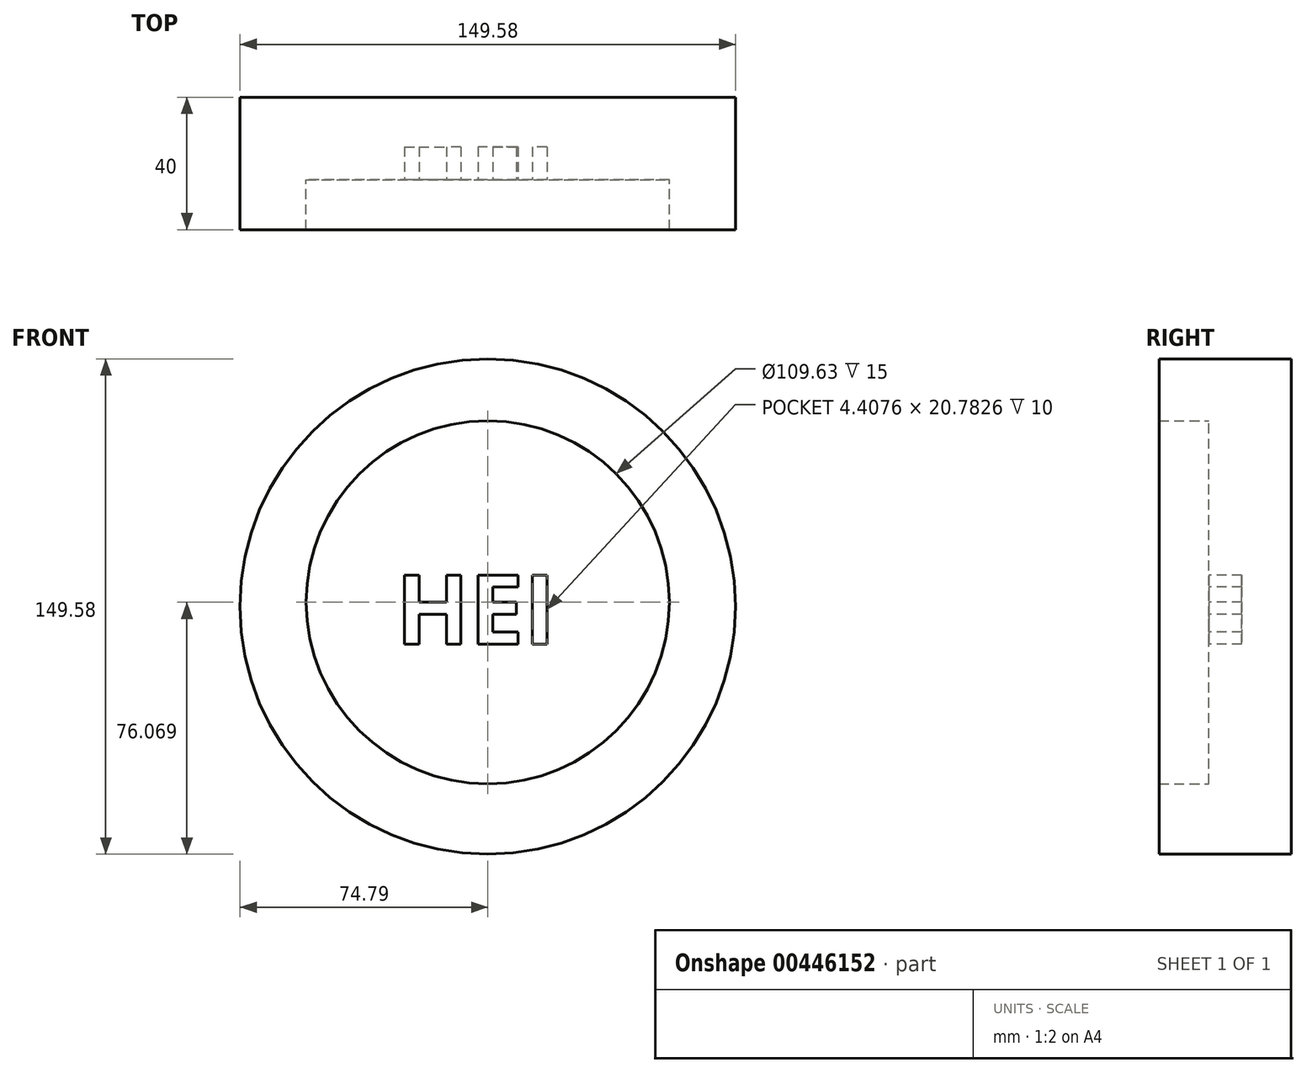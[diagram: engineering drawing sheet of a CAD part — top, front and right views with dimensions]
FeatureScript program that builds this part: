
annotation { "Feature Type Name" : "Feature", "Feature Type Description" : "" }
export const myFeature = defineFeature(function(context is Context, id is Id, definition is map)
    precondition{}
    {
        {
            var Q0;
            Q0=qCreatedBy(makeId("Front.planeOp"),FACE);
            var sketch = newSketch(context, id + "F0", { "sketchPlane" : qUnion([Q0])});
            skCircle(sketch, "E0", {"center": v(0, 0) * mm, "radius": 74.79 * mm});
            skSolve(sketch);
        }
        {
            var Q0;
            Q0 = qSketchRegion(id + "F0", true);
            extrude(context, id + "F1", {"entities" : qUnion([Q0]), "depth" : 25 * mm});
        }
        {
            var Q0;
            Q0=makeQuery(id+"F1.opExtrude","CAP_FACE",FACE,{"disambiguationData":[OSD([sQuery(id+"F0.wireOp",EDGE,"E0")])],"isStart":false});
            var sketch = newSketch(context, id + "F2", { "sketchPlane" : qUnion([Q0])});
            skText(sketch, "E1", { "text": "HEI", "fontName": "OpenSans-Bold.ttf"});
            const initialGuessF2  = {"E1": [-0.02776, -0.01133, 1, 0, 0.02096]};
            skSetInitialGuess(sketch, initialGuessF2);
            skSolve(sketch);
        }
        {
            var Q0;
            Q0 = qSketchRegion(id + "F2", true);
            extrude(context, id + "F3", {"entities" : qUnion([Q0]), "operationType" : NewBodyOperationType.REMOVE, "oppositeDirection" : true, "depth" : 10 * mm});
        }
        {
            var Q0;
            Q0=makeQuery(id+"F1.opExtrude","CAP_FACE",FACE,{"disambiguationData":[OSD([sQuery(id+"F0.wireOp",EDGE,"E0")])],"isStart":false});
            var sketch = newSketch(context, id + "F4", { "sketchPlane" : qUnion([Q0])});
            skCircle(sketch, "E2", {"center": v(0, 1.28) * mm, "radius": 54.81 * mm});
            skSolve(sketch);
        }
        {
            var Q0;
            Q0=makeQuery(id+"F4.imprint","IMPRINT",FACE,{"disambiguationData":[TD([[makeQuery(id+"F4.imprint","IMPRINT",EDGE,{"derivedFrom":sQuery(id+"F4.wireOp",EDGE,"E2")}),-1.0]])]});
            extrude(context, id + "F5", {"entities" : qUnion([Q0]), "operationType" : NewBodyOperationType.ADD, "depth" : 15 * mm});
        }
    });
